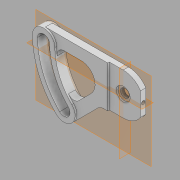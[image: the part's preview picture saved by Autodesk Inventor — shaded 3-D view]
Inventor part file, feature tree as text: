
AUTODESK INVENTOR PART (.ipt)
format: ipt  version: 2020 (Build 240168000, 168)  size: 221,696 bytes
history: native  units: in
note: dims shown in document units (in); Inventor stores cm internally (conversion verified against a paired STEP export)
features: sketch x7, extrude x6, projected_geometry x4, other x1, hole x1
ambient origin geometry x8: Origin, YZ Plane, XZ Plane, XY Plane, X Axis, Y Axis, Z Axis, Center Point
bodies: Body1 (feature_tree)
feature tree (19):
  other  "Sólido1"
  extrude  "Cabezal"  Depth=3.0in
  hole  "Broca y barreno"  [1 undecoded]
  extrude  "Mango"  Depth=1.0in
  extrude  "AgujeroLateral"  Depth=0.5in
  extrude  "BloqueCentral"  Depth=1.62in
  extrude  "HuecoMango"  Depth=0.625in TaperAngle=0.0deg
  extrude  "HuecoCentral"  Depth=0.5in
  sketch  "Boceto1"  dims[d0=3.0in d2=1.25in]
  sketch  "Boceto3"  dims[d3=1.0in d4=0.38in d5=0.0in]
  sketch  "Boceto4"  dims[d6=0.625in d7=0.75in d8=1.0in d9=0.12in d10=0.5635in d11=1.0in d12=0.8108in d14=0.69in]
  sketch  "Boceto8"  dims[d15=0.5in d19=1.62in]
  projected_geometry  "Contorno proyectado2"
  sketch  "Boceto9"  dims[d21=135.0deg d22=1.62in]
  projected_geometry  "Contorno proyectado5"
  sketch  "Boceto10"  dims[d25=0.5in d28=0.625in d29=0.0in]
  projected_geometry  "Contorno proyectado6"
  sketch  "Boceto11"  dims[d36=0.25in d37=0.19in d38=1.6583in d39=0.8292in d40=0.38in d41=0.0in d47=45.0deg d48=0.5in d49=0.5in d50=0.0in d52=0.88in d53=0.88in d54=0.0in d55=0.125in d56=0.0in d57=1.0in d58=1.0in d59=2.0in d60=0.81in d61=0.81in d62=0.5in d63=0.0in]
  projected_geometry  "Contorno proyectado7"
note: 1 required parameter value undecoded (feature->parameter linkage not recoverable at this tier; creation-order binding heuristic only, values carry confidence <= 0.55)
